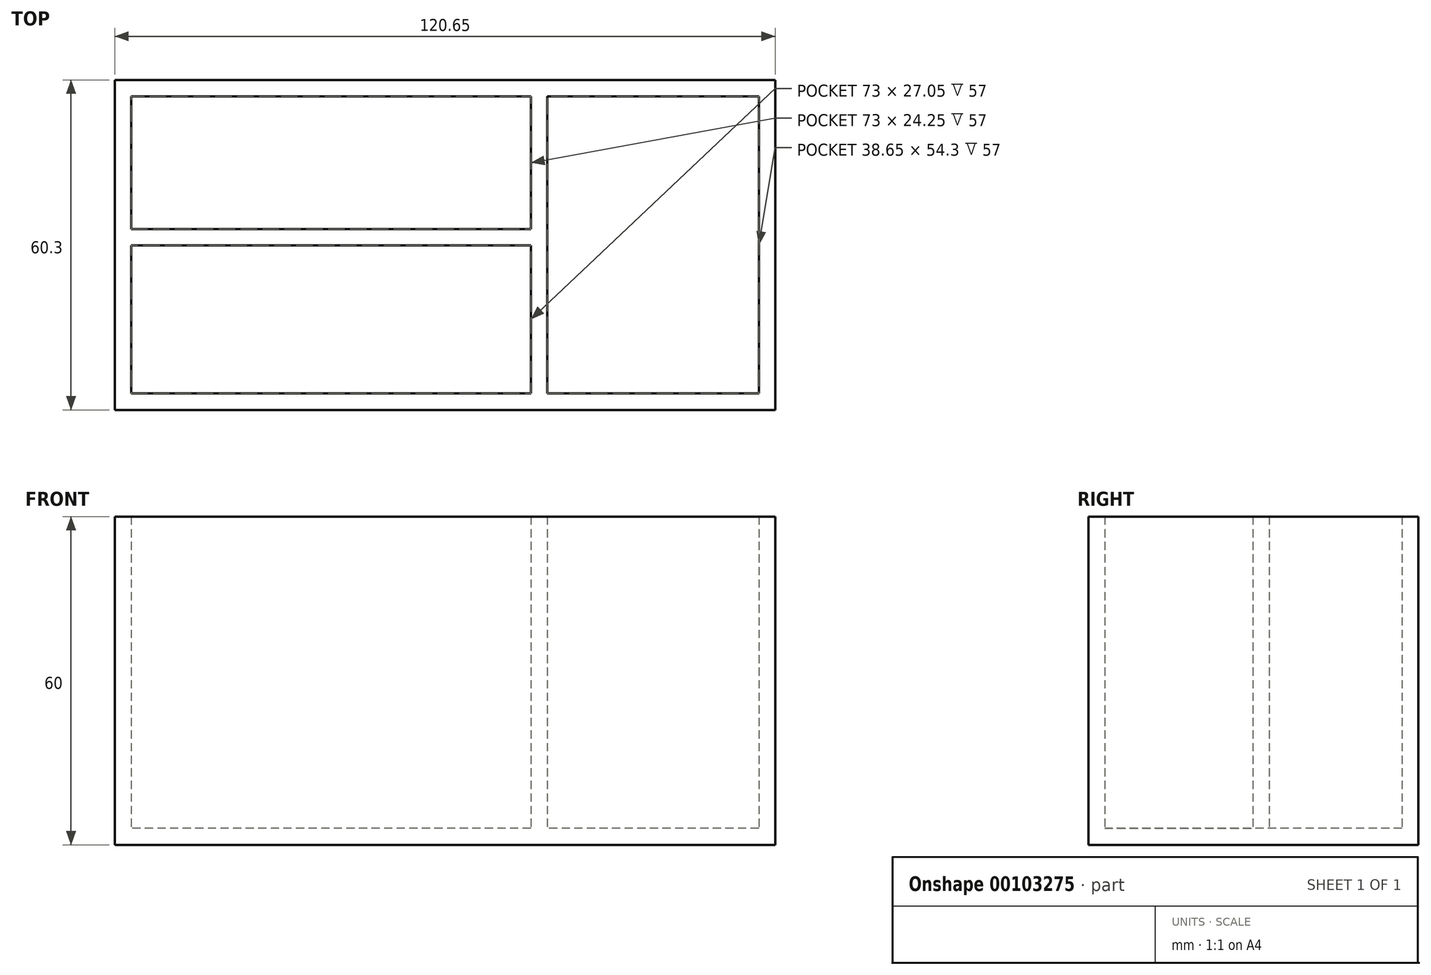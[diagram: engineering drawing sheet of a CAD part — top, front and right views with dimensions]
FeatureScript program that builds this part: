
annotation { "Feature Type Name" : "Feature", "Feature Type Description" : "" }
export const myFeature = defineFeature(function(context is Context, id is Id, definition is map)
    precondition{}
    {
        {
            var Q0;
            Q0=qCreatedBy(makeId("Top.planeOp"),FACE);
            var sketch = newSketch(context, id + "F0", { "sketchPlane" : qUnion([Q0])});
            skLineSegment(sketch, "E0.bottom", {"start": v(0, 0) * mm, "end": v(-120.65, 0) * mm});
            skLineSegment(sketch, "E0.top", {"start": v(0, -60.3) * mm, "end": v(-120.65, -60.3) * mm});
            skLineSegment(sketch, "E0.left", {"start": v(0, 0) * mm, "end": v(0, -60.3) * mm});
            skLineSegment(sketch, "E0.right", {"start": v(-120.65, 0) * mm, "end": v(-120.65, -60.3) * mm});
            skLineSegment(sketch, "E1", {"start": v(-44.65, -57.3) * mm, "end": v(-44.65, -30.25) * mm});
            skLineSegment(sketch, "E2.0", {"start": v(-3, -3) * mm, "end": v(-41.65, -3) * mm});
            skLineSegment(sketch, "E2.1", {"start": v(-3, -3) * mm, "end": v(-3, -57.3) * mm});
            skLineSegment(sketch, "E2.2", {"start": v(-3, -57.3) * mm, "end": v(-41.65, -57.3) * mm});
            skLineSegment(sketch, "E2.3", {"start": v(-117.65, -3) * mm, "end": v(-117.65, -27.25) * mm});
            skLineSegment(sketch, "E3", {"start": v(-117.65, -27.25) * mm, "end": v(-44.65, -27.25) * mm});
            skLineSegment(sketch, "E4", {"start": v(-117.65, -30.25) * mm, "end": v(-44.65, -30.25) * mm});
            skLineSegment(sketch, "E5", {"start": v(-41.65, -3) * mm, "end": v(-41.65, -57.3) * mm});
            skLineSegment(sketch, "E6.trimOffspring", {"start": v(-44.65, -3) * mm, "end": v(-117.65, -3) * mm});
            skLineSegment(sketch, "E7.trimOffspring", {"start": v(-44.65, -57.3) * mm, "end": v(-117.65, -57.3) * mm});
            skLineSegment(sketch, "E8.trimOffspring", {"start": v(-44.65, -27.25) * mm, "end": v(-44.65, -3) * mm});
            skLineSegment(sketch, "E9.trimOffspring", {"start": v(-117.65, -30.25) * mm, "end": v(-117.65, -57.3) * mm});
            skSolve(sketch);
        }
        {
            var Q0;
            Q0=makeQuery(id+"F0.imprint","IMPRINT",FACE,{"disambiguationData":[TD([[makeQuery(id+"F0.imprint","IMPRINT",EDGE,{"derivedFrom":sQuery(id+"F0.wireOp",EDGE,"E0.bottom")}),1.0]])]});
            extrude(context, id + "F1", {"entities" : qUnion([Q0]), "depth" : 57 * mm});
        }
        {
            var Q0;
            Q0=makeQuery(id+"F1.opExtrude","CAP_FACE",FACE,{"disambiguationData":[OSD([sQuery(id+"F0.wireOp",EDGE,"E0.bottom"),sQuery(id+"F0.wireOp",EDGE,"E0.top"),sQuery(id+"F0.wireOp",EDGE,"E0.left"),sQuery(id+"F0.wireOp",EDGE,"E0.right"),sQuery(id+"F0.wireOp",EDGE,"E1"),sQuery(id+"F0.wireOp",EDGE,"E2.0"),sQuery(id+"F0.wireOp",EDGE,"E2.1"),sQuery(id+"F0.wireOp",EDGE,"E2.2"),sQuery(id+"F0.wireOp",EDGE,"E2.3"),sQuery(id+"F0.wireOp",EDGE,"E3"),sQuery(id+"F0.wireOp",EDGE,"E4"),sQuery(id+"F0.wireOp",EDGE,"E5"),sQuery(id+"F0.wireOp",EDGE,"E6.trimOffspring"),sQuery(id+"F0.wireOp",EDGE,"E7.trimOffspring"),sQuery(id+"F0.wireOp",EDGE,"E8.trimOffspring"),sQuery(id+"F0.wireOp",EDGE,"E9.trimOffspring")])],"isStart":true});
            var sketch = newSketch(context, id + "F2", { "sketchPlane" : qUnion([Q0])});
            skLineSegment(sketch, "E10.0", {"start": v(0, 60.3) * mm, "end": v(-120.65, 60.3) * mm});
            skLineSegment(sketch, "E11.0", {"start": v(-120.65, 0) * mm, "end": v(-120.65, 60.3) * mm});
            skLineSegment(sketch, "E12.0", {"start": v(0, 0) * mm, "end": v(0, 60.3) * mm});
            skLineSegment(sketch, "E13.0", {"start": v(0, 0) * mm, "end": v(-120.65, 0) * mm});
            skSolve(sketch);
        }
        {
            var Q0;
            Q0=makeQuery(id+"F2.imprint","IMPRINT",FACE,{"disambiguationData":[TD([[makeQuery(id+"F2.imprint","IMPRINT",EDGE,{"derivedFrom":sQuery(id+"F2.wireOp",EDGE,"E10.0")}),1.0]])]});
            var Q1;
            Q1=makeQuery(id+"F2.imprint","IMPRINT",FACE,{"disambiguationData":[TD([[makeQuery(id+"F2.imprint","IMPRINT",EDGE,{"derivedFrom":makeQuery(id+"F1.opExtrude","CAP_EDGE",EDGE,{"disambiguationData":[OSD([sQuery(id+"F0.wireOp",EDGE,"E1")])],"isStart":true})}),-1.0]])]});
            var Q2;
            Q2=makeQuery(id+"F2.imprint","IMPRINT",FACE,{"disambiguationData":[TD([[makeQuery(id+"F2.imprint","IMPRINT",EDGE,{"derivedFrom":makeQuery(id+"F1.opExtrude","CAP_EDGE",EDGE,{"disambiguationData":[OSD([sQuery(id+"F0.wireOp",EDGE,"E2.3")])],"isStart":true})}),-1.0]])]});
            var Q3;
            Q3=makeQuery(id+"F2.imprint","IMPRINT",FACE,{"disambiguationData":[TD([[makeQuery(id+"F2.imprint","IMPRINT",EDGE,{"derivedFrom":makeQuery(id+"F1.opExtrude","CAP_EDGE",EDGE,{"disambiguationData":[OSD([sQuery(id+"F0.wireOp",EDGE,"E2.0")])],"isStart":true})}),-1.0]])]});
            extrude(context, id + "F3", {"entities" : qUnion([Q0, Q1, Q2, Q3]), "operationType" : NewBodyOperationType.ADD, "depth" : 3 * mm});
        }
    });
